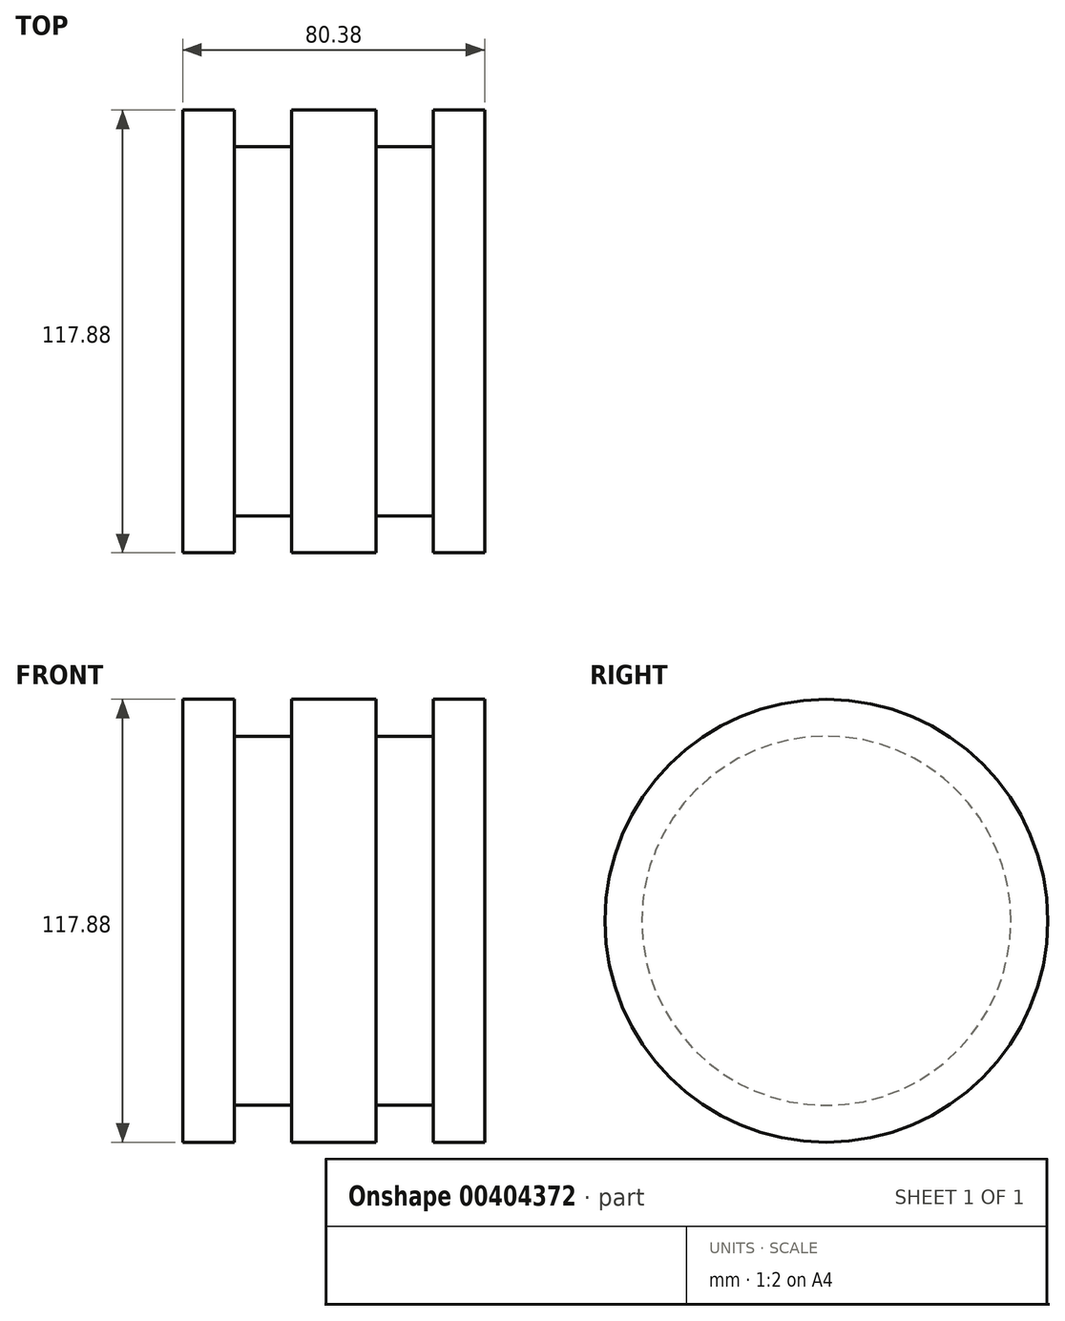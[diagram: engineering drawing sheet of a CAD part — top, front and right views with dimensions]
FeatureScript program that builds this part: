
annotation { "Feature Type Name" : "Feature", "Feature Type Description" : "" }
export const myFeature = defineFeature(function(context is Context, id is Id, definition is map)
    precondition{}
    {
        {
            var Q0;
            Q0=qCreatedBy(makeId("Front.planeOp"),FACE);
            var sketch = newSketch(context, id + "F0", { "sketchPlane" : qUnion([Q0])});
            skLineSegment(sketch, "E0", {"start": v(-40.19, 0) * mm, "end": v(-40.19, 58.94) * mm});
            skLineSegment(sketch, "E1", {"start": v(-40.19, 58.94) * mm, "end": v(-26.47, 58.94) * mm});
            skLineSegment(sketch, "E2", {"start": v(-26.47, 58.94) * mm, "end": v(-26.47, 49.13) * mm});
            skLineSegment(sketch, "E3", {"start": v(-26.47, 49.13) * mm, "end": v(-11.27, 49.13) * mm});
            skLineSegment(sketch, "E4", {"start": v(-11.27, 49.13) * mm, "end": v(-11.27, 58.94) * mm});
            skLineSegment(sketch, "E5", {"start": v(-11.27, 58.94) * mm, "end": v(0, 58.94) * mm});
            skLineSegment(sketch, "E6", {"start": v(0, 58.94) * mm, "end": v(0, 0) * mm});
            skLineSegment(sketch, "E7", {"start": v(0, 0) * mm, "end": v(-40.19, 0) * mm});
            skSolve(sketch);
        }
        {
            var Q0;
            Q0 = qSketchRegion(id + "F0", true);
            var Q1;
            Q1=sQuery(id+"F0.wireOp",EDGE,"E7");
            revolve(context, id + "F1", {"entities" : qUnion([Q0]), "axis" : qUnion([Q1]), "revolveType" : RevolveType.FULL});
        }
        {
            var Q0;
            Q0=makeQuery(id+"F1.opRevolve","SWEPT_BODY",BODY,{"disambiguationData":[OSD([sQuery(id+"F0.wireOp",EDGE,"E0"),sQuery(id+"F0.wireOp",EDGE,"E1"),sQuery(id+"F0.wireOp",EDGE,"E2"),sQuery(id+"F0.wireOp",EDGE,"E3"),sQuery(id+"F0.wireOp",EDGE,"E4"),sQuery(id+"F0.wireOp",EDGE,"E5"),sQuery(id+"F0.wireOp",EDGE,"E6"),sQuery(id+"F0.wireOp",EDGE,"E7")])]});
            var Q1;
            Q1=qCreatedBy(makeId("Right.planeOp"),FACE);
            mirror(context, id + "F2", {"operationType" : NewBodyOperationType.ADD, "entities" : qUnion([Q0]), "mirrorPlane" : qUnion([Q1])});
        }
    });
